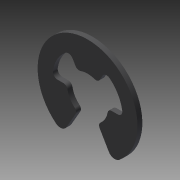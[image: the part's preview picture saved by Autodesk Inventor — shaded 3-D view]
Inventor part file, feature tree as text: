
AUTODESK INVENTOR PART (.ipt)
format: ipt  version: 2014 (Build 180170000, 170)  size: 138,752 bytes
history: native  units: in
note: dims shown in document units (in); Inventor stores cm internally (conversion verified against a paired STEP export)
features: other x7, extrude x1, sketch x1
ambient origin geometry x8: Origin, YZ Plane, XZ Plane, XY Plane, X Axis, Y Axis, Z Axis, Center Point
bodies: Solid1 (feature_tree)
feature tree (9):
  extrude  "Extrusion1"  [1 undecoded]
  other  "RR_XY"
  other  "RR_YZ"
  other  "RR_ZX"
  other  "RR_X"
  other  "RR_Y"
  other  "RR_Z"
  other  "RR_Center"
  sketch  "Sketch_1"  dims[d0=0.0365in d1=0.0in]
note: 1 required parameter value undecoded (feature->parameter linkage not recoverable at this tier; creation-order binding heuristic only, values carry confidence <= 0.55)
